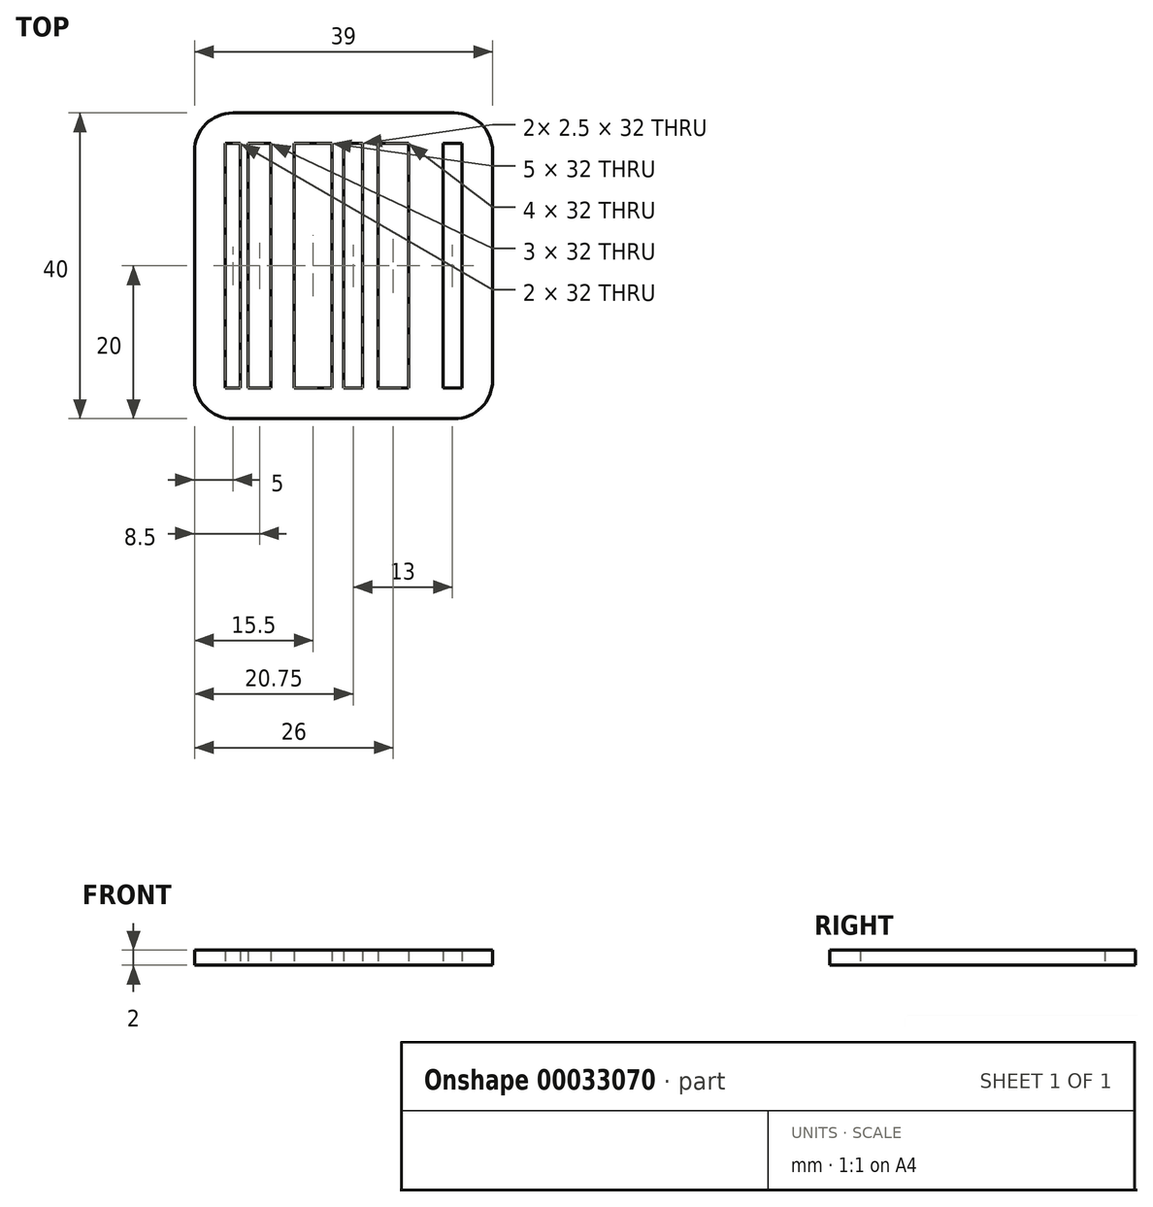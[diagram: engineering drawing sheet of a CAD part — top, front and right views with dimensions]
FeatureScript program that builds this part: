
annotation { "Feature Type Name" : "Feature", "Feature Type Description" : "" }
export const myFeature = defineFeature(function(context is Context, id is Id, definition is map)
    precondition{}
    {
        {
            var Q0;
            Q0=qCreatedBy(makeId("Top.planeOp"),FACE);
            var sketch = newSketch(context, id + "F0", { "sketchPlane" : qUnion([Q0])});
            skLineSegment(sketch, "E0", {"start": v(0, 0) * mm, "end": v(0, 40) * mm});
            skLineSegment(sketch, "E1", {"start": v(0, 40) * mm, "end": v(39, 40) * mm});
            skLineSegment(sketch, "E2", {"start": v(39, 40) * mm, "end": v(39, 0) * mm});
            skLineSegment(sketch, "E3", {"start": v(39, 0) * mm, "end": v(0, 0) * mm});
            skLineSegment(sketch, "E4.bottom", {"start": v(4, 4) * mm, "end": v(6, 4) * mm});
            skLineSegment(sketch, "E4.top", {"start": v(4, 36) * mm, "end": v(6, 36) * mm});
            skLineSegment(sketch, "E4.left", {"start": v(4, 4) * mm, "end": v(4, 36) * mm});
            skLineSegment(sketch, "E4.right", {"start": v(6, 4) * mm, "end": v(6, 36) * mm});
            skLineSegment(sketch, "E5.bottom", {"start": v(7, 4) * mm, "end": v(10, 4) * mm});
            skLineSegment(sketch, "E5.top", {"start": v(7, 36) * mm, "end": v(10, 36) * mm});
            skLineSegment(sketch, "E5.left", {"start": v(7, 4) * mm, "end": v(7, 36) * mm});
            skLineSegment(sketch, "E5.right", {"start": v(10, 4) * mm, "end": v(10, 36) * mm});
            skLineSegment(sketch, "E6", {"start": v(0, 4) * mm, "end": v(39, 4) * mm, "construction": true});
            skLineSegment(sketch, "E7", {"start": v(0, 36) * mm, "end": v(39, 36) * mm, "construction": true});
            skLineSegment(sketch, "E8.bottom", {"start": v(13, 36) * mm, "end": v(18, 36) * mm});
            skLineSegment(sketch, "E8.top", {"start": v(13, 4) * mm, "end": v(18, 4) * mm});
            skLineSegment(sketch, "E8.left", {"start": v(13, 36) * mm, "end": v(13, 4) * mm});
            skLineSegment(sketch, "E8.right", {"start": v(18, 36) * mm, "end": v(18, 4) * mm});
            skLineSegment(sketch, "E9.bottom", {"start": v(21, 4) * mm, "end": v(19.5, 4) * mm});
            skLineSegment(sketch, "E9.top", {"start": v(21, 36) * mm, "end": v(19.5, 36) * mm});
            skLineSegment(sketch, "E9.left", {"start": v(21, 4) * mm, "end": v(21, 36) * mm});
            skLineSegment(sketch, "E9.right", {"start": v(19.5, 4) * mm, "end": v(19.5, 36) * mm});
            skLineSegment(sketch, "E10.bottom", {"start": v(21, 4) * mm, "end": v(22, 4) * mm});
            skLineSegment(sketch, "E10.top", {"start": v(21, 36) * mm, "end": v(22, 36) * mm});
            skLineSegment(sketch, "E10.right", {"start": v(22, 4) * mm, "end": v(22, 36) * mm});
            skLineSegment(sketch, "E11.bottom", {"start": v(35, 36) * mm, "end": v(32.5, 36) * mm});
            skLineSegment(sketch, "E11.top", {"start": v(35, 4) * mm, "end": v(32.5, 4) * mm});
            skLineSegment(sketch, "E11.left", {"start": v(35, 36) * mm, "end": v(35, 4) * mm});
            skLineSegment(sketch, "E11.right", {"start": v(32.5, 36) * mm, "end": v(32.5, 4) * mm});
            skLineSegment(sketch, "E12.bottom", {"start": v(24, 4) * mm, "end": v(28, 4) * mm});
            skLineSegment(sketch, "E12.top", {"start": v(24, 36) * mm, "end": v(28, 36) * mm});
            skLineSegment(sketch, "E12.left", {"start": v(24, 4) * mm, "end": v(24, 36) * mm});
            skLineSegment(sketch, "E12.right", {"start": v(28, 4) * mm, "end": v(28, 36) * mm});
            skSolve(sketch);
        }
        {
            var Q0;
            Q0=makeQuery(id+"F0.imprint","IMPRINT",FACE,{"disambiguationData":[TD([[makeQuery(id+"F0.imprint","IMPRINT",EDGE,{"derivedFrom":sQuery(id+"F0.wireOp",EDGE,"E0")}),-1.0]])]});
            extrude(context, id + "F1", {"entities" : qUnion([Q0]), "depth" : 2 * mm});
        }
        {
            var Q0;
            Q0=makeQuery(id+"F1.opExtrude","SWEPT_EDGE",EDGE,{"disambiguationData":[OSD([sQuery(id+"F0.wireOp",EDGE,"E1"),sQuery(id+"F0.wireOp",EDGE,"E2")])]});
            var Q1;
            Q1=makeQuery(id+"F1.opExtrude","SWEPT_EDGE",EDGE,{"disambiguationData":[OSD([sQuery(id+"F0.wireOp",EDGE,"E2"),sQuery(id+"F0.wireOp",EDGE,"E3")])]});
            var Q2;
            Q2=makeQuery(id+"F1.opExtrude","SWEPT_EDGE",EDGE,{"disambiguationData":[OSD([sQuery(id+"F0.wireOp",EDGE,"E0"),sQuery(id+"F0.wireOp",EDGE,"E3")])]});
            var Q3;
            Q3=makeQuery(id+"F1.opExtrude","SWEPT_EDGE",EDGE,{"disambiguationData":[OSD([sQuery(id+"F0.wireOp",EDGE,"E0"),sQuery(id+"F0.wireOp",EDGE,"E1")])]});
            fillet(context, id + "F2", {"entities" : qUnion([Q0, Q1, Q2, Q3]), "radius" : 5 * mm, "tangentPropagation" : true, "allowEdgeOverflow" : false});
        }
    });
